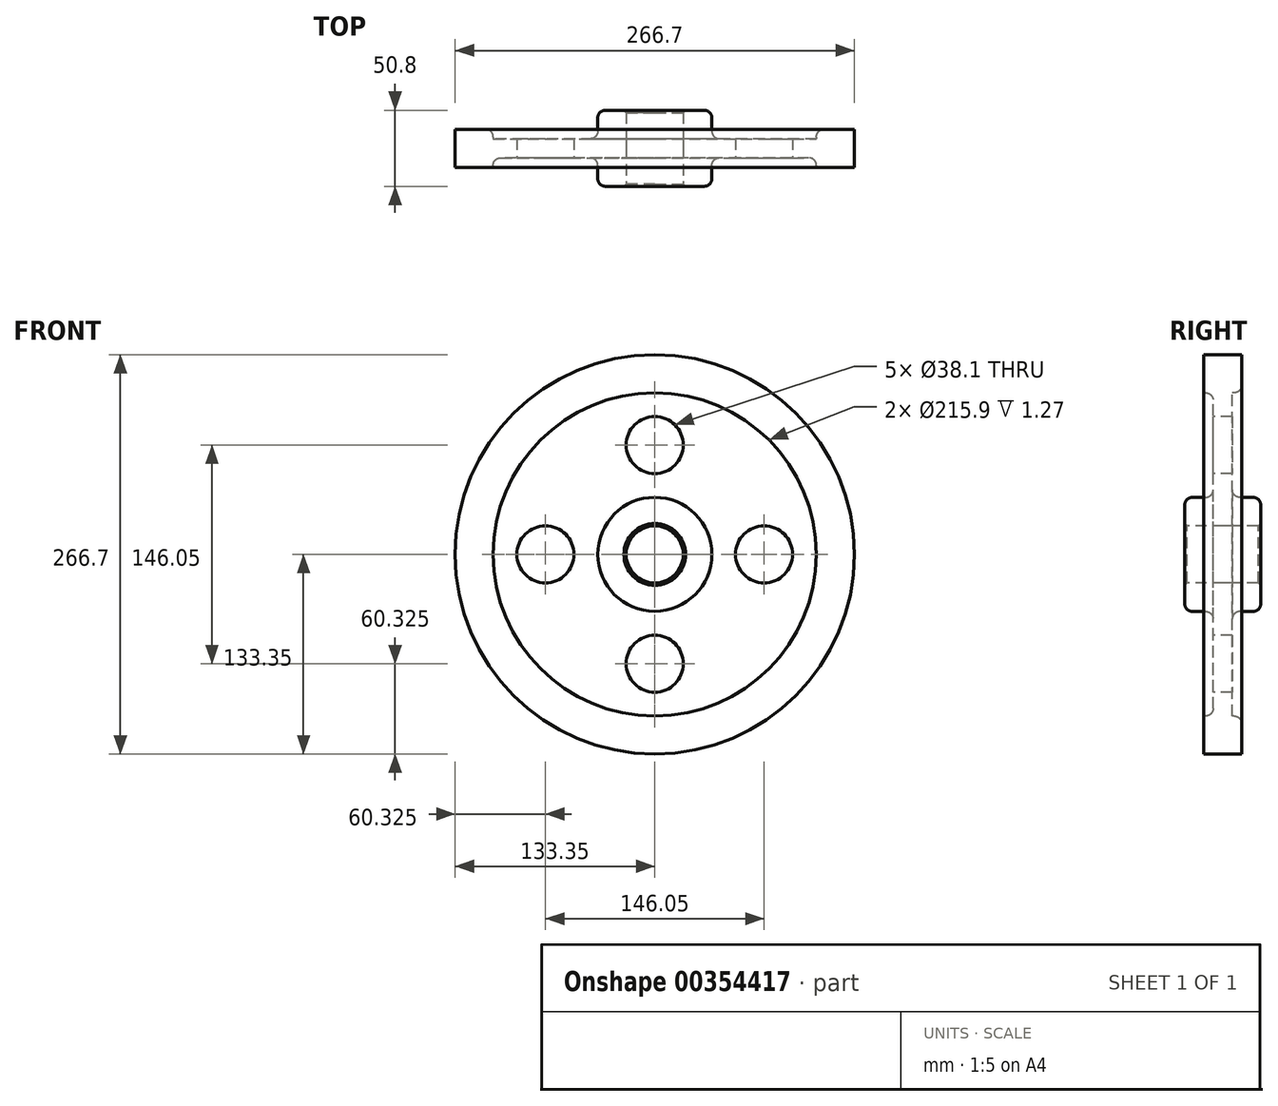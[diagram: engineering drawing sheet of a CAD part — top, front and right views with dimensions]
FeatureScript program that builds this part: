
annotation { "Feature Type Name" : "Feature", "Feature Type Description" : "" }
export const myFeature = defineFeature(function(context is Context, id is Id, definition is map)
    precondition{}
    {
        {
            var Q0;
            Q0=qCreatedBy(makeId("Right.planeOp"),FACE);
            var sketch = newSketch(context, id + "F0", { "sketchPlane" : qUnion([Q0])});
            skLineSegment(sketch, "E0", {"start": v(0, 0) * mm, "end": v(76.2, 0) * mm, "construction": true});
            skLineSegment(sketch, "E1.0", {"start": v(6.35, 38.1) * mm, "end": v(25.4, 38.1) * mm});
            skLineSegment(sketch, "E2.0", {"start": v(6.35, 107.95) * mm, "end": v(12.7, 107.95) * mm});
            skLineSegment(sketch, "E3.0", {"start": v(0, 133.35) * mm, "end": v(12.7, 133.35) * mm});
            skLineSegment(sketch, "E4", {"start": v(0, 133.35) * mm, "end": v(0, 0) * mm, "construction": true});
            skLineSegment(sketch, "E5.0", {"start": v(25.4, 19.05) * mm, "end": v(76.2, 19.05) * mm});
            skLineSegment(sketch, "E6.MirrorCS", {"start": v(-6.35, 107.95) * mm, "end": v(-12.7, 107.95) * mm});
            skLineSegment(sketch, "E7.MirrorCS", {"start": v(-6.35, 38.1) * mm, "end": v(-25.4, 38.1) * mm});
            skLineSegment(sketch, "E8.MirrorCS", {"start": v(0, 133.35) * mm, "end": v(-12.7, 133.35) * mm});
            skLineSegment(sketch, "E9", {"start": v(25.4, 19.05) * mm, "end": v(-25.4, 19.05) * mm});
            skLineSegment(sketch, "E10", {"start": v(-12.7, 133.35) * mm, "end": v(-12.7, 107.95) * mm});
            skLineSegment(sketch, "E11", {"start": v(12.7, 133.35) * mm, "end": v(12.7, 107.95) * mm});
            skLineSegment(sketch, "E12", {"start": v(-6.35, 38.1) * mm, "end": v(-6.35, 107.95) * mm});
            skLineSegment(sketch, "E13", {"start": v(6.35, 107.95) * mm, "end": v(6.35, 38.1) * mm});
            skLineSegment(sketch, "E14", {"start": v(25.4, 19.05) * mm, "end": v(25.4, 38.1) * mm});
            skLineSegment(sketch, "E15", {"start": v(-25.4, 38.1) * mm, "end": v(-25.4, 19.05) * mm});
            skLineSegment(sketch, "E16.MirrorCS", {"start": v(0, 0) * mm, "end": v(-76.2, 0) * mm, "construction": true});
            skSolve(sketch);
        }
        {
            var Q0;
            Q0 = qSketchRegion(id + "F0", true);
            var Q1;
            Q1=sQuery(id+"F0.wireOp",EDGE,"E0");
            revolve(context, id + "F1", {"entities" : qUnion([Q0]), "axis" : qUnion([Q1]), "revolveType" : RevolveType.FULL});
        }
        {
            var Q0;
            Q0=makeQuery(id+"F1.opRevolve","SWEPT_FACE",FACE,{"disambiguationData":[OSD([sQuery(id+"F0.wireOp",EDGE,"E12")])]});
            var sketch = newSketch(context, id + "F2", { "sketchPlane" : qUnion([Q0])});
            skLineSegment(sketch, "E17", {"start": v(0, 0) * mm, "end": v(0, 73.03) * mm});
            skCircle(sketch, "E18", {"center": v(0, 73.03) * mm, "radius": 19.05 * mm});
            skCircle(sketch, "E19.1.0", {"center": v(-73.03, 0) * mm, "radius": 19.05 * mm});
            skCircle(sketch, "E19.2.0", {"center": v(0, -73.03) * mm, "radius": 19.05 * mm});
            skCircle(sketch, "E19.3.0", {"center": v(73.03, 0) * mm, "radius": 19.05 * mm});
            skPoint(sketch, "E19.center", {"position": v(0, 0) * mm});
            skSolve(sketch);
        }
        {
            var Q0;
            Q0=makeQuery(id+"F2.imprint","IMPRINT",FACE,{"disambiguationData":[TD([[makeQuery(id+"F2.imprint","IMPRINT",EDGE,{"derivedFrom":sQuery(id+"F2.wireOp",EDGE,"E19.3.0")}),1.0]])]});
            var Q1;
            Q1=makeQuery(id+"F2.imprint","IMPRINT",FACE,{"disambiguationData":[TD([[makeQuery(id+"F2.imprint","IMPRINT",EDGE,{"derivedFrom":sQuery(id+"F2.wireOp",EDGE,"E19.2.0")}),1.0]])]});
            var Q2;
            Q2=makeQuery(id+"F2.imprint","IMPRINT",FACE,{"disambiguationData":[TD([[makeQuery(id+"F2.imprint","IMPRINT",EDGE,{"derivedFrom":sQuery(id+"F2.wireOp",EDGE,"E19.1.0")}),1.0]])]});
            var Q3;
            Q3=makeQuery(id+"F2.imprint","IMPRINT",FACE,{"disambiguationData":[TD([[makeQuery(id+"F2.imprint","IMPRINT",EDGE,{"derivedFrom":sQuery(id+"F2.wireOp",EDGE,"E18")}),1.0]])]});
            extrude(context, id + "F3", {"entities" : qUnion([Q0, Q1, Q2, Q3]), "operationType" : NewBodyOperationType.REMOVE, "oppositeDirection" : true, "depth" : 25.4 * mm});
        }
        {
            var Q0;
            Q0=makeQuery(id+"F1.opRevolve","SWEPT_EDGE",EDGE,{"disambiguationData":[OSD([sQuery(id+"F0.wireOp",EDGE,"E6.MirrorCS"),sQuery(id+"F0.wireOp",EDGE,"E12")])]});
            var Q1;
            Q1=makeQuery(id+"F1.opRevolve","SWEPT_EDGE",EDGE,{"disambiguationData":[OSD([sQuery(id+"F0.wireOp",EDGE,"E7.MirrorCS"),sQuery(id+"F0.wireOp",EDGE,"E12")])]});
            var Q2;
            Q2=makeQuery(id+"F1.opRevolve","SWEPT_EDGE",EDGE,{"disambiguationData":[OSD([sQuery(id+"F0.wireOp",EDGE,"E7.MirrorCS"),sQuery(id+"F0.wireOp",EDGE,"E15")])]});
            var Q3;
            Q3=makeQuery(id+"F1.opRevolve","SWEPT_EDGE",EDGE,{"disambiguationData":[OSD([sQuery(id+"F0.wireOp",EDGE,"E2.0"),sQuery(id+"F0.wireOp",EDGE,"E11")])]});
            var Q4;
            Q4=makeQuery(id+"F1.opRevolve","SWEPT_EDGE",EDGE,{"disambiguationData":[OSD([sQuery(id+"F0.wireOp",EDGE,"E1.0"),sQuery(id+"F0.wireOp",EDGE,"E14")])]});
            var Q5;
            Q5=makeQuery(id+"F1.opRevolve","SWEPT_EDGE",EDGE,{"disambiguationData":[OSD([sQuery(id+"F0.wireOp",EDGE,"E1.0"),sQuery(id+"F0.wireOp",EDGE,"E13")])]});
            fillet(context, id + "F4", {"entities" : qUnion([Q0, Q1, Q2, Q3, Q4, Q5]), "radius" : 5.08 * mm, "tangentPropagation" : true, "allowEdgeOverflow" : false});
        }
        {
            var Q0;
            Q0=makeQuery(id+"F1.opRevolve","SWEPT_EDGE",EDGE,{"disambiguationData":[OSD([sQuery(id+"F0.wireOp",EDGE,"E9"),sQuery(id+"F0.wireOp",EDGE,"E15")])]});
            var Q1;
            Q1=makeQuery(id+"F1.opRevolve","SWEPT_EDGE",EDGE,{"disambiguationData":[OSD([sQuery(id+"F0.wireOp",EDGE,"E9"),sQuery(id+"F0.wireOp",EDGE,"E14")])]});
            chamfer(context, id + "F5", {"entities" : qUnion([Q0, Q1]), "width" : 1.59 * mm, "tangentPropagation" : true});
        }
    });
